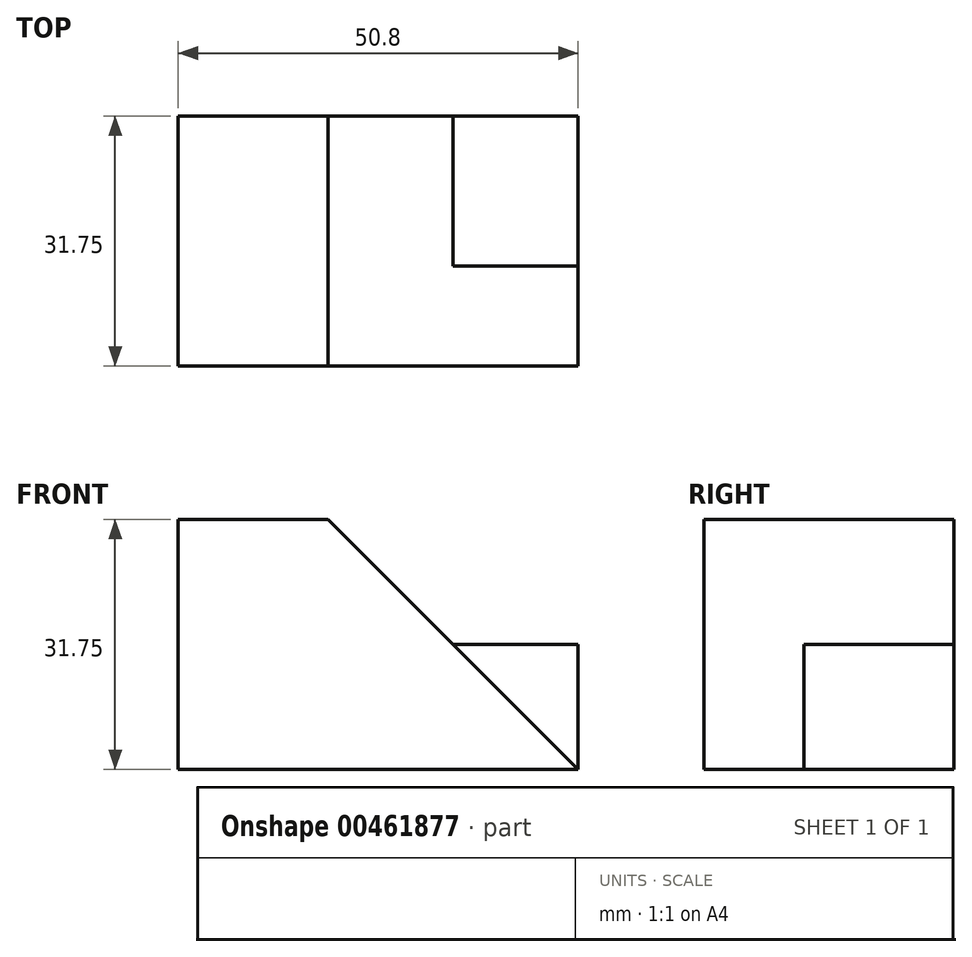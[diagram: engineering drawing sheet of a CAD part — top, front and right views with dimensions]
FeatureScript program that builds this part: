
annotation { "Feature Type Name" : "Feature", "Feature Type Description" : "" }
export const myFeature = defineFeature(function(context is Context, id is Id, definition is map)
    precondition{}
    {
        {
            var Q0;
            Q0=qCreatedBy(makeId("Front.planeOp"),FACE);
            var sketch = newSketch(context, id + "F0", { "sketchPlane" : qUnion([Q0])});
            skLineSegment(sketch, "E0.bottom", {"start": v(0, 0) * mm, "end": v(50.8, 0) * mm});
            skLineSegment(sketch, "E0.top", {"start": v(0, 31.75) * mm, "end": v(50.8, 31.75) * mm});
            skLineSegment(sketch, "E0.left", {"start": v(0, 0) * mm, "end": v(0, 31.75) * mm});
            skLineSegment(sketch, "E0.right", {"start": v(50.8, 0) * mm, "end": v(50.8, 31.75) * mm});
            skSolve(sketch);
        }
        {
            var Q0;
            Q0=makeQuery(id+"F0.imprint","IMPRINT",FACE,{"disambiguationData":[TD([[makeQuery(id+"F0.imprint","IMPRINT",EDGE,{"derivedFrom":sQuery(id+"F0.wireOp",EDGE,"E0.bottom")}),1.0]])]});
            extrude(context, id + "F1", {"entities" : qUnion([Q0]), "depth" : 31.75 * mm});
        }
        {
            var Q0;
            Q0=makeQuery(id+"F1.opExtrude","CAP_FACE",FACE,{"disambiguationData":[OSD([sQuery(id+"F0.wireOp",EDGE,"E0.bottom"),sQuery(id+"F0.wireOp",EDGE,"E0.top"),sQuery(id+"F0.wireOp",EDGE,"E0.left"),sQuery(id+"F0.wireOp",EDGE,"E0.right")])],"isStart":false});
            var sketch = newSketch(context, id + "F2", { "sketchPlane" : qUnion([Q0])});
            skLineSegment(sketch, "E1", {"start": v(50.8, 0) * mm, "end": v(19.05, 31.75) * mm});
            skLineSegment(sketch, "E2", {"start": v(50.8, 0) * mm, "end": v(50.8, 15.87) * mm});
            skLineSegment(sketch, "E3", {"start": v(50.8, 15.87) * mm, "end": v(34.93, 15.87) * mm});
            skSolve(sketch);
        }
        {
            var Q0;
            {var subQ3=sQuery(id+"F2.wireOp",EDGE,"E3");Q0=makeQuery(id+"F2.imprint","IMPRINT",FACE,{"disambiguationData":[TD([[makeQuery(id+"F2.imprint","IMPRINT",EDGE,{"derivedFrom":subQ3}),-1.0]])]});}
            extrude(context, id + "F3", {"entities" : qUnion([Q0]), "operationType" : NewBodyOperationType.REMOVE, "oppositeDirection" : true, "depth" : 31.75 * mm});
        }
        {
            var Q0;
            Q0=makeQuery(id+"F1.opExtrude","CAP_FACE",FACE,{"disambiguationData":[OSD([sQuery(id+"F0.wireOp",EDGE,"E0.bottom"),sQuery(id+"F0.wireOp",EDGE,"E0.top"),sQuery(id+"F0.wireOp",EDGE,"E0.left"),sQuery(id+"F0.wireOp",EDGE,"E0.right")])],"isStart":false});
            var sketch = newSketch(context, id + "F4", { "sketchPlane" : qUnion([Q0])});
            skLineSegment(sketch, "E4", {"start": v(50.8, 0) * mm, "end": v(34.93, 15.87) * mm});
            skLineSegment(sketch, "E5", {"start": v(34.93, 15.87) * mm, "end": v(34.93, 0) * mm});
            skSolve(sketch);
        }
        {
            var Q0;
            Q0=makeQuery(id+"F4.imprint","IMPRINT",FACE,{"disambiguationData":[TD([[makeQuery(id+"F4.imprint","IMPRINT",EDGE,{"derivedFrom":sQuery(id+"F4.wireOp",EDGE,"E4")}),-1.0]])]});
            extrude(context, id + "F5", {"entities" : qUnion([Q0]), "operationType" : NewBodyOperationType.REMOVE, "oppositeDirection" : true, "depth" : 12.7 * mm});
        }
    });
